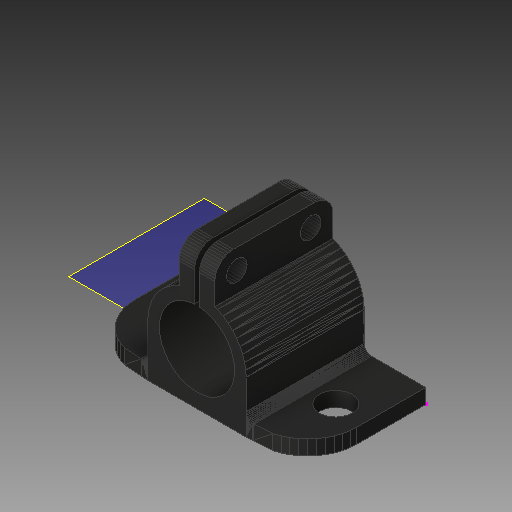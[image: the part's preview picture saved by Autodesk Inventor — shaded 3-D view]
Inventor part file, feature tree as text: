
AUTODESK INVENTOR PART (.ipt)
format: ipt  version: 2018 (Build 220112000, 112)  size: 671,744 bytes
history: native  units: mm
features: sketch x5, other x2, plane x2, extrude x2
ambient origin geometry x8: Origin, YZ Plane, XZ Plane, XY Plane, X Axis, Y Axis, Z Axis, Center Point
bodies: Solid1 (feature_tree)
feature tree (11):
  other  "12mm Rod Holder_fixed"
  plane  "Work Plane1"
  sketch  "Sketch2"  dims[d0=5.3mm d1=5.3mm]
  plane  "Work Plane2"
  sketch  "Sketch3"  dims[d2=10.0mm d3=0.0mm d4=12.2mm]
  other  "MeshFeature1"
  sketch  "Sketch4"  dims[d5=10.0mm d6=0.0mm]
  extrude  "Extrusion1"  Depth=5.3mm
  extrude  "Extrusion2"  Depth=10.0mm
  sketch  "Sketch5"
  sketch  "Sketch6"
